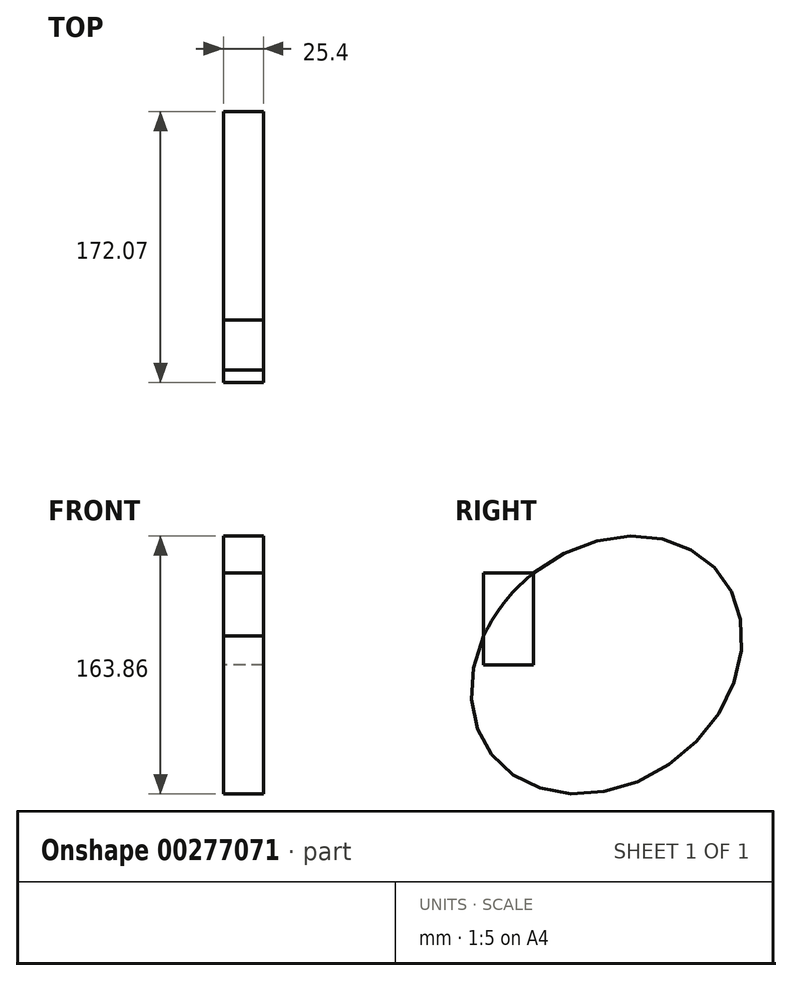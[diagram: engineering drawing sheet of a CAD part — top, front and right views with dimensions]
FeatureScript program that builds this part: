
annotation { "Feature Type Name" : "Feature", "Feature Type Description" : "" }
export const myFeature = defineFeature(function(context is Context, id is Id, definition is map)
    precondition{}
    {
        {
            var Q0;
            Q0=qCreatedBy(makeId("Right.planeOp"),FACE);
            var sketch = newSketch(context, id + "F0", { "sketchPlane" : qUnion([Q0])});
            skLineSegment(sketch, "E0.bottom", {"start": v(-43.52, 58.42) * mm, "end": v(-75.27, 58.42) * mm});
            skLineSegment(sketch, "E0.top", {"start": v(-43.52, 0) * mm, "end": v(-75.27, 0) * mm});
            skLineSegment(sketch, "E0.left", {"start": v(-43.52, 58.42) * mm, "end": v(-43.52, 0) * mm});
            skLineSegment(sketch, "E0.right", {"start": v(-75.27, 58.42) * mm, "end": v(-75.27, 0) * mm});
            skEllipse(sketch, "E1", {"center": v(2.74, 0) * mm, "majorRadius": 74.52 * mm, "minorRadius": 92.52 * mm, "majorAxis": v(-0.62, 0.78)});
            skSolve(sketch);
        }
        {
            var Q0;
            {var subQ0=sQuery(id+"F0.wireOp",EDGE,"E0.bottom");Q0=makeQuery(id+"F0.imprint","IMPRINT",FACE,{"disambiguationData":[TD([[makeQuery(id+"F0.imprint","IMPRINT",EDGE,{"derivedFrom":subQ0}),1.0]])]});}
            var Q1;
            {var subQ0=sQuery(id+"F0.wireOp",EDGE,"E0.top");Q1=makeQuery(id+"F0.imprint","IMPRINT",FACE,{"disambiguationData":[TD([[makeQuery(id+"F0.imprint","IMPRINT",EDGE,{"derivedFrom":subQ0}),1.0]])]});}
            extrude(context, id + "F1", {"entities" : qUnion([Q0, Q1]), "depth" : 25.4 * mm});
        }
    });
